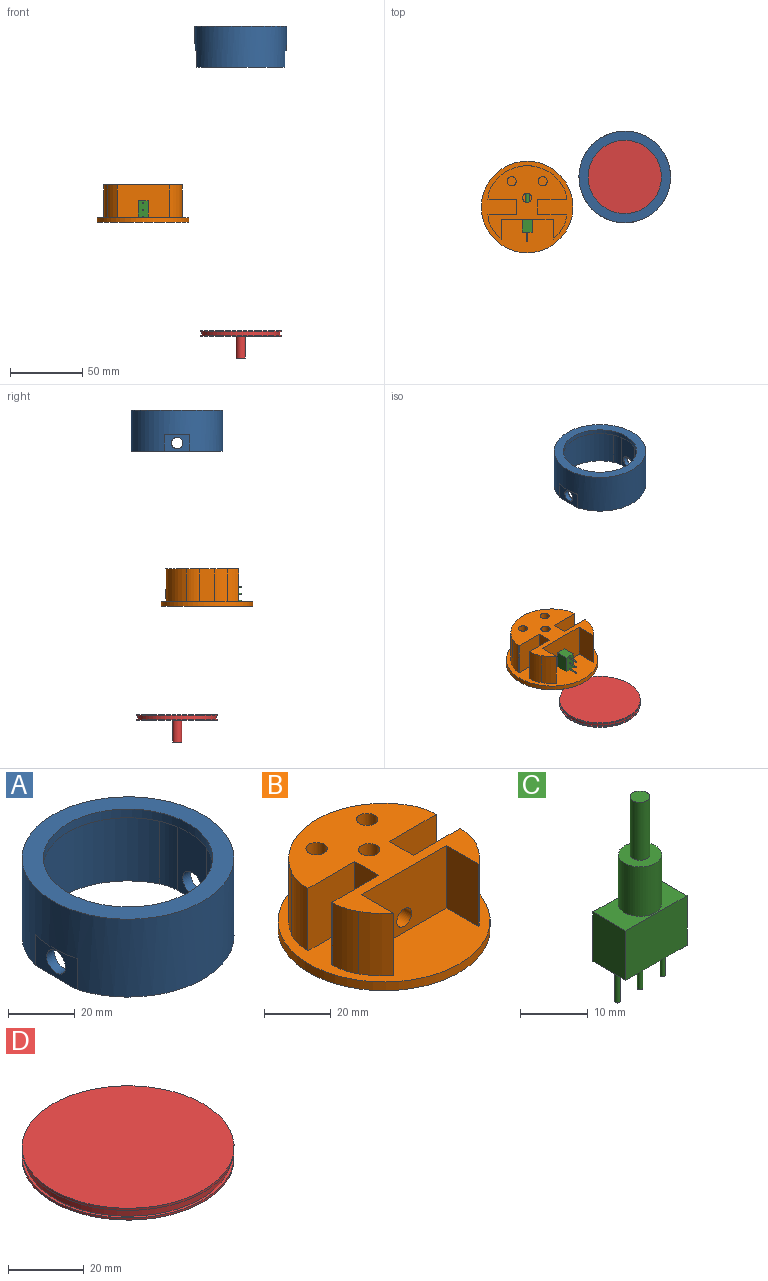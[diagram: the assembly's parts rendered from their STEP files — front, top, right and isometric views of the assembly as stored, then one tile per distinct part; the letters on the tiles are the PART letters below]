
ASSEMBLY  parts=4 mates=2
PART A: 19 faces, bbox 63.5x63.5x28.6 mm
  f0: cylinder r=28.57mm len=51.6mm, axis (0,0,1), area 1635.2mm2, adj f2,f3,f15,f18
  f1: cylinder r=31.75mm len=63.5mm, axis (0,0,-1), area 5288.5mm2, adj f2,f5,f7,f8,f9,f10
  f2: plane 63.5x60.96mm, normal (0,0,-1), area 607.3mm2, adj f0,f1,f6,f8,f10,f11,f12,f15
  f3: plane 57.15x54.31mm, normal (0,0,-1), area 502.6mm2, adj f0,f4,f6,f11,f12,f15,f16,f17
  f4: cylinder r=25.4mm len=50.8mm, axis (0,0,-1), area 506.7mm2, adj f3,f5
  f5: plane 63.5x63.5mm, normal (0,0,1), area 1140.1mm2, adj f1,f4
  f6: cylinder r=28.57mm len=51.6mm, axis (0,0,1), area 1635.2mm2, adj f2,f3,f16,f17
  f7: plane 17.78x1.27mm, normal (0,0,-1), area 15.1mm2, adj f1,f8
  f8: plane 17.78x11.43mm, normal (-1,0,0), area 153mm2, adj f1,f2,f7,f14
  f9: plane 17.78x1.27mm, normal (0,0,-1), area 15.1mm2, adj f1,f10
  f10: plane 17.78x11.43mm, normal (1,0,0), area 153mm2, adj f1,f2,f9,f13
  f11: plane 25.4x12.56mm, normal (1,0,0), area 268.6mm2, adj f2,f3,f14,f17,f18
  f12: plane 25.4x12.56mm, normal (-1,0,0), area 268.6mm2, adj f2,f3,f13,f15,f16
  f13: cylinder r=4mm len=8mm, axis (1,0,0), area 83.5mm2, adj f10,f12
  f14: cylinder r=4mm len=8mm, axis (1,0,0), area 83.5mm2, adj f8,f11
  f15: cylinder r=13.97mm len=25.4mm, axis (0,0,1), area 157.7mm2, adj f0,f2,f3,f12
  f16: cylinder r=13.97mm len=25.4mm, axis (0,0,1), area 157.7mm2, adj f2,f3,f6,f12
  f17: cylinder r=13.97mm len=25.4mm, axis (0,0,1), area 157.7mm2, adj f2,f3,f6,f11
  f18: cylinder r=13.97mm len=25.4mm, axis (0,0,1), area 157.7mm2, adj f0,f2,f3,f11
PART B: 33 faces, bbox 63.5x63.5x26 mm
  f0: cylinder r=3.17mm len=17.39mm, axis (0,0,-1), area 306.5mm2, adj f22,f29,f32
  f1: plane 63.5x63.5mm, normal (0,0,1), area 1691.5mm2, adj f2,f4,f5,f6,f7,f8,f9,f10
  f2: cylinder r=31.75mm len=63.5mm, axis (0,0,-1), area 633.4mm2, adj f1,f3
  f3: plane 63.5x63.5mm, normal (0,0,-1), area 3166.9mm2, adj f2
  f4: plane 22.86x19.85mm, normal (0,-1,0), area 453.8mm2, adj f1,f5,f20,f22
  f5: plane 22.86x0.27mm, normal (1,0,0), area 6.1mm2, adj f1,f4,f22,f25
  f6: cylinder r=28.57mm len=49.64mm, axis (0,0,-1), area 1343.2mm2, adj f1,f22,f25,f26,f29
  f7: plane 22.86x0.27mm, normal (-1,0,0), area 6.1mm2, adj f1,f8,f22,f26
  f8: plane 22.86x19.85mm, normal (0,-1,0), area 453.8mm2, adj f1,f7,f9,f22
  f9: plane 22.86x10.16mm, normal (-1,0,0), area 232.3mm2, adj f1,f8,f10,f22
  f10: plane 22.86x19.85mm, normal (0,1,0), area 453.8mm2, adj f1,f9,f11,f22
  f11: plane 22.86x0.27mm, normal (-1,0,0), area 6.1mm2, adj f1,f10,f22,f27
  f12: cylinder r=28.57mm len=22.86mm, axis (0,0,-1), area 242.2mm2, adj f1,f13,f22,f27
  f13: plane 22.86x13.64mm, normal (1,0,0), area 311.9mm2, adj f1,f12,f14,f22
  f14: plane 36.01x22.86mm, normal (0,-1,0), area 791.5mm2, adj f1,f13,f15,f22,f32
  f15: plane 22.86x13.64mm, normal (-1,0,0), area 311.9mm2, adj f1,f14,f16,f22
  f16: cylinder r=28.57mm len=22.86mm, axis (0,0,-1), area 242.2mm2, adj f1,f15,f22,f28
  f17: plane 22.86x0.27mm, normal (1,0,0), area 6.1mm2, adj f1,f18,f22,f28
  f18: plane 22.86x19.85mm, normal (0,1,0), area 453.8mm2, adj f1,f17,f20,f22
  f19: cylinder r=3.17mm len=22.86mm, axis (0,0,-1), area 456mm2, adj f22,f23
  f20: plane 22.86x10.16mm, normal (1,0,0), area 232.3mm2, adj f1,f4,f18,f22
  f21: cylinder r=3.17mm len=22.86mm, axis (0,0,-1), area 456mm2, adj f22,f24
  f22: plane 54.31x50.77mm, normal (0,0,1), area 1380.4mm2, adj f0,f4,f5,f6,f7,f8,f9,f10
  f23: plane 6.35x6.35mm, normal (0,0,1), area 31.7mm2, adj f19
  f24: plane 6.35x6.35mm, normal (0,0,1), area 31.7mm2, adj f21
  f25: cylinder r=17.78mm len=22.86mm, axis (0,0,-1), area 210.7mm2, adj f1,f5,f6,f22
  f26: cylinder r=17.78mm len=22.86mm, axis (0,0,-1), area 210.7mm2, adj f1,f6,f7,f22
  f27: cylinder r=17.78mm len=22.86mm, axis (0,0,-1), area 210.7mm2, adj f1,f11,f12,f22
  f28: cylinder r=17.78mm len=22.86mm, axis (0,0,-1), area 210.7mm2, adj f1,f16,f17,f22
  f29: cylinder r=3.17mm len=22.21mm, axis (0,-1,0), area 401mm2, adj f0,f6,f31
  f30: plane 6.35x6.35mm, normal (0,0,1), area 31.7mm2, adj f31
  f31: cylinder r=3.17mm len=6.35mm, axis (0,0,-1), area 68.9mm2, adj f29,f30,f32
  f32: cylinder r=3.17mm len=14.91mm, axis (0,-1,0), area 257.1mm2, adj f0,f14,f31
PART C: 16 faces, bbox 12.7x6.9x34.5 mm
  f0: plane 12.7x8.89mm, normal (0,-1,0), area 112.9mm2, adj f1,f3,f4,f5
  f1: plane 8.89x6.86mm, normal (1,0,0), area 61mm2, adj f0,f2,f4,f5
  f2: plane 12.7x8.89mm, normal (0,1,0), area 112.9mm2, adj f1,f3,f4,f5
  f3: plane 8.89x6.86mm, normal (-1,0,0), area 61mm2, adj f0,f2,f4,f5
  f4: plane 12.7x6.86mm, normal (0,0,1), area 55.4mm2, adj f0,f1,f2,f3,f12
  f5: plane 12.7x6.86mm, normal (0,0,-1), area 85.7mm2, adj f0,f1,f2,f3,f6,f8,f10
  f6: cylinder r=0.38mm len=6.35mm, axis (0,0,1), area 15.2mm2, adj f5,f7
  f7: plane 0.76x0.76mm, normal (0,0,-1), area 0.5mm2, adj f6
  f8: cylinder r=0.38mm len=6.35mm, axis (0,0,1), area 15.2mm2, adj f5,f9
  f9: plane 0.76x0.76mm, normal (0,0,-1), area 0.5mm2, adj f8
  f10: cylinder r=0.38mm len=6.35mm, axis (0,0,1), area 15.2mm2, adj f5,f11
  f11: plane 0.76x0.76mm, normal (0,0,-1), area 0.5mm2, adj f10
  f12: cylinder r=3.17mm len=8.89mm, axis (0,0,-1), area 177.3mm2, adj f4,f13
  f13: plane 6.35x6.35mm, normal (0,0,1), area 25mm2, adj f12,f14
  f14: cylinder r=1.46mm len=10.41mm, axis (0,0,-1), area 95.6mm2, adj f13,f15
  f15: plane 2.92x2.92mm, normal (0,0,1), area 6.7mm2, adj f14
PART D: 9 faces, bbox 55.9x55.9x19.1 mm
  f0: plane 55.88x55.88mm, normal (0,0,-1), area 2420.8mm2, adj f1,f7
  f1: cylinder r=27.94mm len=55.88mm, axis (0,0,1), area 121.5mm2, adj f0,f2
  f2: plane 55.88x55.88mm, normal (0,0,1), area 136.3mm2, adj f1,f3
  f3: cylinder r=27.15mm len=54.31mm, axis (0,0,1), area 413.8mm2, adj f2,f4
  f4: plane 55.88x55.88mm, normal (0,0,-1), area 136.3mm2, adj f3,f5
  f5: cylinder r=27.94mm len=55.88mm, axis (0,0,1), area 121.5mm2, adj f4,f6
  f6: plane 55.88x55.88mm, normal (0,0,1), area 2452.5mm2, adj f5
  f7: cylinder r=3.17mm len=15.24mm, axis (0,0,1), area 304mm2, adj f0,f8
  f8: plane 6.35x6.35mm, normal (0,0,-1), area 31.7mm2, adj f7
PLACE A rot(axis=(0,0,-1),0deg) t=(24.82,80,143.05)mm
PLACE B t=(-42.81,59.35,10.08)mm
PLACE C rot(axis=(-0.58,0.58,0.58),120deg) t=(-42.81,41.91,18.73)mm
PLACE D t=(24.82,80,-66.74)mm
MATE cylindrical D.f1 <-> A.f0  axis (0,0,1) through (24.82,80,-66.74)mm
MATE fastened B.f29 <-> C.f12  axis (0,-1,0) through (-42.81,50.8,18.73)mm
